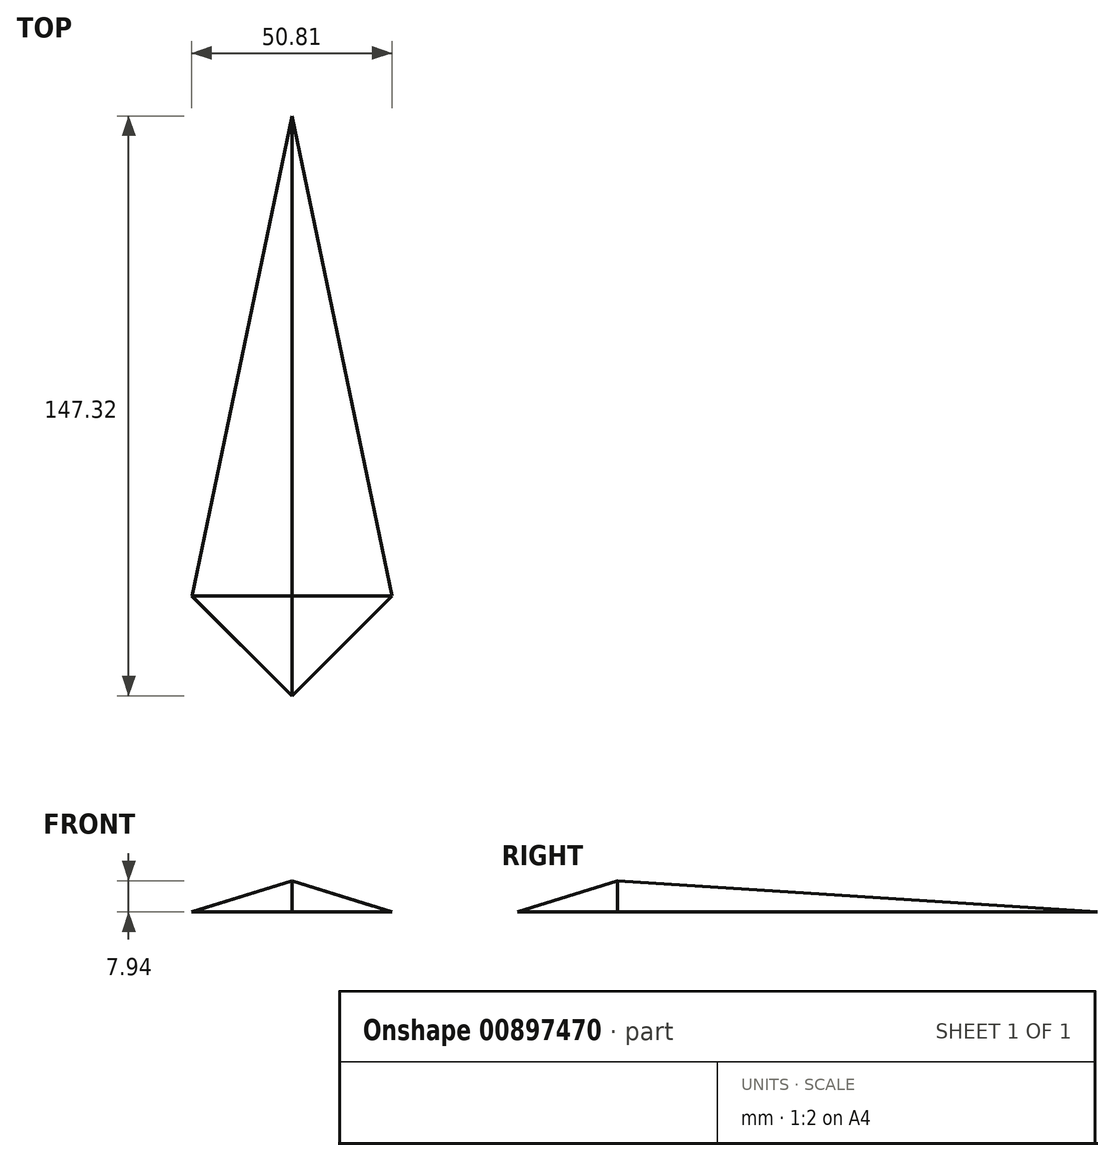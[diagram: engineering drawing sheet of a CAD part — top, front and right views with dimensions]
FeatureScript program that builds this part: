
annotation { "Feature Type Name" : "Feature", "Feature Type Description" : "" }
export const myFeature = defineFeature(function(context is Context, id is Id, definition is map)
    precondition{}
    {
        {
            var Q0;
            Q0=qCreatedBy(makeId("Top.planeOp"),FACE);
            var sketch = newSketch(context, id + "F0", { "sketchPlane" : qUnion([Q0])});
            skLineSegment(sketch, "E0", {"start": v(0, 0) * mm, "end": v(-25.4, 0) * mm});
            skLineSegment(sketch, "E1", {"start": v(0, 0) * mm, "end": v(0, 121.92) * mm});
            skLineSegment(sketch, "E2", {"start": v(0, 121.92) * mm, "end": v(-25.4, 0) * mm});
            skLineSegment(sketch, "E3", {"start": v(0, 0) * mm, "end": v(0, -25.4) * mm});
            skLineSegment(sketch, "E4", {"start": v(0, -25.4) * mm, "end": v(-25.4, 0) * mm});
            skLineSegment(sketch, "E5", {"start": v(-6.35, -19.05) * mm, "end": v(-6.35, -120.65) * mm});
            skLineSegment(sketch, "E6", {"start": v(0, -120.65) * mm, "end": v(0, -25.4) * mm});
            skArc(sketch, "E7", {"start": v(0, -119.15) * mm, "mid": v(-14.2, -133.35) * mm, "end": v(0, -147.55) * mm});
            skArc(sketch, "E8", {"start": v(0, -123.62) * mm, "mid": v(-9.73, -133.35) * mm, "end": v(0, -143.08) * mm});
            skLineSegment(sketch, "E9.left", {"start": v(0, -119.15) * mm, "end": v(0, -147.55) * mm});
            skLineSegment(sketch, "E10.MirrorCS", {"start": v(0, 121.92) * mm, "end": v(25.4, 0) * mm});
            skLineSegment(sketch, "E11.MirrorCS", {"start": v(0, -25.4) * mm, "end": v(25.4, 0) * mm});
            skLineSegment(sketch, "E12.MirrorCS", {"start": v(6.35, -19.05) * mm, "end": v(6.35, -120.65) * mm});
            skArc(sketch, "E13.MirrorCS", {"start": v(0, -119.15) * mm, "mid": v(14.2, -133.35) * mm, "end": v(0, -147.55) * mm});
            skArc(sketch, "E14.MirrorCS", {"start": v(0, -123.62) * mm, "mid": v(9.73, -133.35) * mm, "end": v(0, -143.08) * mm});
            skLineSegment(sketch, "E15.MirrorCS", {"start": v(0, 0) * mm, "end": v(25.4, 0) * mm});
            skSolve(sketch);
        }
        {
            var Q0;
            Q0=qCreatedBy(makeId("Right.planeOp"),FACE);
            var sketch = newSketch(context, id + "F1", { "sketchPlane" : qUnion([Q0])});
            skLineSegment(sketch, "E16", {"start": v(0, 0) * mm, "end": v(0, 7.94) * mm});
            skLineSegment(sketch, "E17", {"start": v(-25.38, 0) * mm, "end": v(0, 7.94) * mm});
            skLineSegment(sketch, "E18", {"start": v(121.92, 0) * mm, "end": v(0, 7.94) * mm});
            skLineSegment(sketch, "E19", {"start": v(121.92, 0) * mm, "end": v(0, 0) * mm});
            skLineSegment(sketch, "E20", {"start": v(0, 0) * mm, "end": v(-25.38, 0) * mm});
            skLineSegment(sketch, "E21.MirrorCS", {"start": v(121.92, 0) * mm, "end": v(0, -7.94) * mm});
            skLineSegment(sketch, "E22.MirrorCS", {"start": v(-25.38, 0) * mm, "end": v(0, -7.94) * mm});
            skSolve(sketch);
        }
        {
            var Q0;
            Q0=sQuery(id+"F1.wireOp",VERTEX,"E16.end");
            var Q1;
            Q1=sQuery(id+"F0.wireOp",VERTEX,"E1.end");
            var Q2;
            Q2=sQuery(id+"F0.wireOp",VERTEX,"E0.end");
            cPlane(context, id + "F2", {"entities" : qUnion([Q0, Q1, Q2]), "cplaneType" : CPlaneType.THREE_POINT, "offset" : 25.4 * mm, "width" : 152.4 * mm, "height" : 152.4 * mm});
        }
        {
            var Q0;
            Q0=sQuery(id+"F0.wireOp",VERTEX,"E10.MirrorCS.end");
            var Q1;
            Q1=sQuery(id+"F1.wireOp",VERTEX,"E16.end");
            var Q2;
            Q2=sQuery(id+"F0.wireOp",VERTEX,"E1.end");
            cPlane(context, id + "F3", {"entities" : qUnion([Q0, Q1, Q2]), "cplaneType" : CPlaneType.THREE_POINT, "offset" : 25.4 * mm, "width" : 152.4 * mm, "height" : 152.4 * mm});
        }
        {
            var Q0;
            Q0=qCreatedBy(id+"F3.planeOp",FACE);
            var sketch = newSketch(context, id + "F4", { "sketchPlane" : qUnion([Q0])});
            skLineSegment(sketch, "E23", {"start": v(24.25, 0) * mm, "end": v(-2.35, 121.65) * mm});
            skLineSegment(sketch, "E24", {"start": v(-2.35, 121.65) * mm, "end": v(-2.35, -0.53) * mm});
            skLineSegment(sketch, "E25", {"start": v(-2.35, -0.53) * mm, "end": v(24.25, 0) * mm});
            skSolve(sketch);
        }
        {
            var Q0;
            Q0=qCreatedBy(id+"F2.planeOp",FACE);
            var sketch = newSketch(context, id + "F5", { "sketchPlane" : qUnion([Q0])});
            skLineSegment(sketch, "E26", {"start": v(-24.25, 0) * mm, "end": v(2.36, -121.66) * mm});
            skLineSegment(sketch, "E27", {"start": v(2.36, -121.66) * mm, "end": v(2.36, 0.53) * mm});
            skLineSegment(sketch, "E28", {"start": v(2.36, 0.53) * mm, "end": v(-24.25, 0) * mm});
            skSolve(sketch);
        }
        {
            var Q0;
            Q0=makeQuery(id+"F0.imprint","IMPRINT",FACE,{"disambiguationData":[TD([[makeQuery(id+"F0.imprint","IMPRINT",EDGE,{"derivedFrom":sQuery(id+"F0.wireOp",EDGE,"E1")}),-1.0]])]});
            var Q1;
            Q1=makeQuery(id+"F4.imprint","IMPRINT",FACE,{"disambiguationData":[TD([[makeQuery(id+"F4.imprint","IMPRINT",EDGE,{"derivedFrom":sQuery(id+"F4.wireOp",EDGE,"E23")}),1.0]])]});
            var Q2;
            Q2=makeQuery(id+"F5.imprint","IMPRINT",FACE,{"disambiguationData":[TD([[makeQuery(id+"F5.imprint","IMPRINT",EDGE,{"derivedFrom":sQuery(id+"F5.wireOp",EDGE,"E26")}),1.0]])]});
            var Q3;
            Q3=makeQuery(id+"F0.imprint","IMPRINT",FACE,{"disambiguationData":[TD([[makeQuery(id+"F0.imprint","IMPRINT",EDGE,{"derivedFrom":sQuery(id+"F0.wireOp",EDGE,"E0")}),-1.0]])]});
            extrude(context, id + "F6", {"entities" : qUnion([Q0, Q1, Q2, Q3]), "depth" : 0 * mm, "offsetDistance" : 25.4 * mm, "hasSecondDirection" : true, "secondDirectionOppositeDirection" : true, "secondDirectionDepth" : 0 * mm});
        }
        {
            var Q0;
            Q0=sQuery(id+"F0.wireOp",VERTEX,"E0.end");
            var Q1;
            Q1=sQuery(id+"F1.wireOp",VERTEX,"E16.end");
            var Q2;
            Q2=sQuery(id+"F0.wireOp",VERTEX,"E3.end");
            cPlane(context, id + "F7", {"entities" : qUnion([Q0, Q1, Q2]), "cplaneType" : CPlaneType.THREE_POINT, "offset" : 25.4 * mm, "width" : 152.4 * mm, "height" : 152.4 * mm});
        }
        {
            var Q0;
            Q0=sQuery(id+"F1.wireOp",VERTEX,"E16.end");
            var Q1;
            Q1=sQuery(id+"F0.wireOp",VERTEX,"E10.MirrorCS.end");
            var Q2;
            Q2=sQuery(id+"F0.wireOp",VERTEX,"E3.end");
            cPlane(context, id + "F8", {"entities" : qUnion([Q0, Q1, Q2]), "cplaneType" : CPlaneType.THREE_POINT, "offset" : 25.4 * mm, "width" : 152.4 * mm, "height" : 152.4 * mm});
        }
        {
            var Q0;
            Q0=qCreatedBy(id+"F7.planeOp",FACE);
            var sketch = newSketch(context, id + "F9", { "sketchPlane" : qUnion([Q0])});
            skLineSegment(sketch, "E29", {"start": v(-24.35, 0) * mm, "end": v(2.16, -24.24) * mm});
            skLineSegment(sketch, "E30", {"start": v(2.16, -24.24) * mm, "end": v(2.16, 2.35) * mm});
            skLineSegment(sketch, "E31", {"start": v(2.16, 2.35) * mm, "end": v(-24.35, 0) * mm});
            skSolve(sketch);
        }
        {
            var Q0;
            Q0=qCreatedBy(id+"F8.planeOp",FACE);
            var sketch = newSketch(context, id + "F10", { "sketchPlane" : qUnion([Q0])});
            skLineSegment(sketch, "E32", {"start": v(24.34, 0) * mm, "end": v(-2.17, -24.24) * mm});
            skLineSegment(sketch, "E33", {"start": v(-2.17, -24.24) * mm, "end": v(-2.17, 2.37) * mm});
            skLineSegment(sketch, "E34", {"start": v(-2.17, 2.37) * mm, "end": v(24.34, 0) * mm});
            skSolve(sketch);
        }
        {
            var Q0;
            {var subQ0=sQuery(id+"F0.wireOp",EDGE,"E0");Q0=makeQuery(id+"F0.imprint","IMPRINT",FACE,{"disambiguationData":[TD([[makeQuery(id+"F0.imprint","IMPRINT",EDGE,{"derivedFrom":subQ0}),1.0]])]});}
            var Q1;
            {var subQ0=sQuery(id+"F0.wireOp",EDGE,"E3");Q1=makeQuery(id+"F0.imprint","IMPRINT",FACE,{"disambiguationData":[TD([[makeQuery(id+"F0.imprint","IMPRINT",EDGE,{"derivedFrom":subQ0}),1.0]])]});}
            var Q2;
            Q2=makeQuery(id+"F9.imprint","IMPRINT",FACE,{"disambiguationData":[TD([[makeQuery(id+"F9.imprint","IMPRINT",EDGE,{"derivedFrom":sQuery(id+"F9.wireOp",EDGE,"E29")}),1.0]])]});
            var Q3;
            Q3=makeQuery(id+"F10.imprint","IMPRINT",FACE,{"disambiguationData":[TD([[makeQuery(id+"F10.imprint","IMPRINT",EDGE,{"derivedFrom":sQuery(id+"F10.wireOp",EDGE,"E32")}),-1.0]])]});
            extrude(context, id + "F11", {"entities" : qUnion([Q0, Q1, Q2, Q3]), "depth" : 0 * mm, "offsetDistance" : 25.4 * mm, "hasSecondDirection" : true, "secondDirectionOppositeDirection" : true, "secondDirectionDepth" : 0 * mm});
        }
    });
